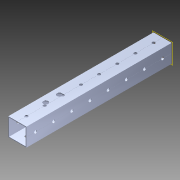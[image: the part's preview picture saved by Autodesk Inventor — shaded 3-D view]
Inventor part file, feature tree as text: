
AUTODESK INVENTOR PART (.ipt)
format: ipt  version: 2014 (Build 180170000, 170)  size: 1,223,168 bytes
history: native  units: in
note: dims shown in document units (in); Inventor stores cm internally (conversion verified against a paired STEP export)
features: extrude x2, pattern_circular x1, other x1, plane x1, imported_body x1, sketch x1, reference x1
ambient origin geometry x8: Origin, YZ Plane, XZ Plane, XY Plane, X Axis, Y Axis, Z Axis, Center Point
bodies: Body1 (feature_tree)
feature tree (8):
  pattern_circular  "CirPattern2"
  other  "217-3426-STEP1"
  plane  "Work Plane1"
  extrude  "Extrusion1"  Depth=0.135in TaperAngle=0.0deg
  extrude  "Extrusion2"  Depth=0.135in TaperAngle=0.0deg
  imported_body  "Base1"
  sketch  "Sketch1"  dims[d0=-8.0in d1=3937.0079in d2=0.0in d3=3.937in d4=0.0in d5=0.135in d6=0.27in d7=0.27in d8=2.0in d9=2.0in]
  reference  "Reference1"
